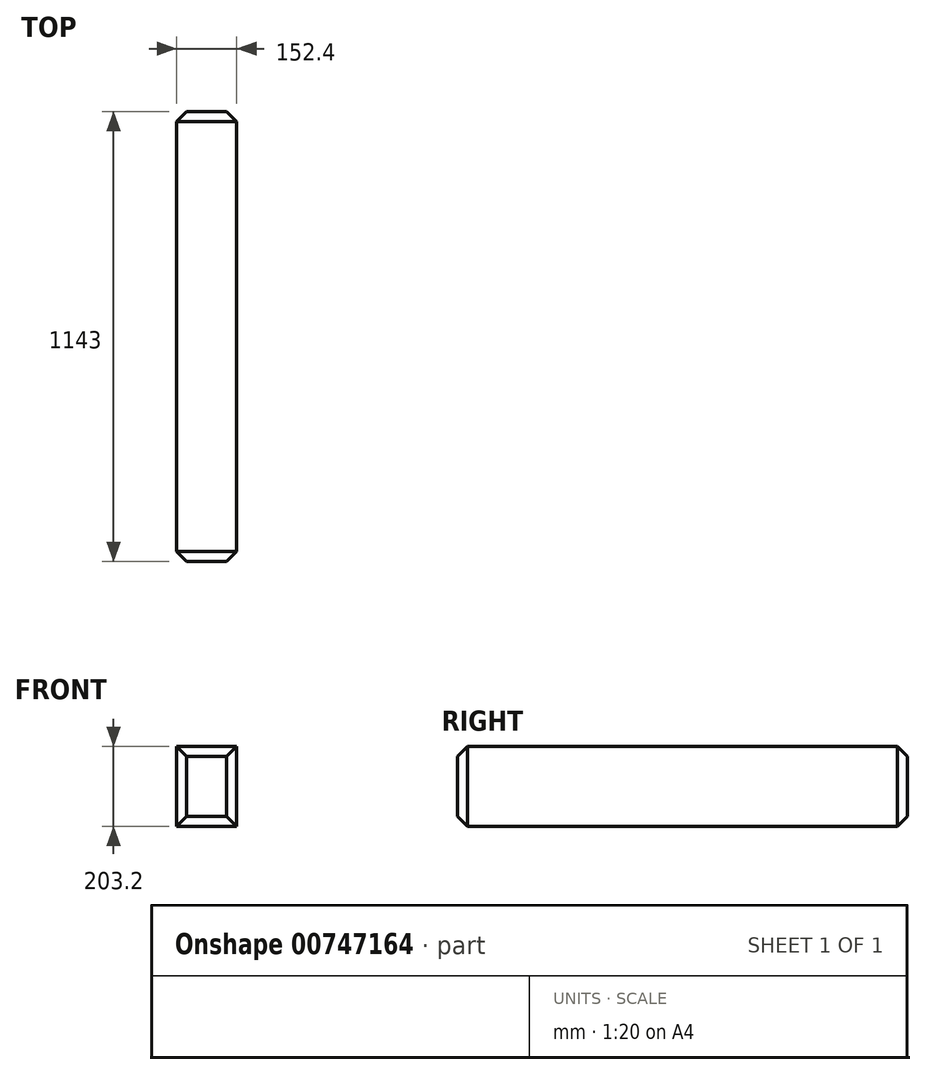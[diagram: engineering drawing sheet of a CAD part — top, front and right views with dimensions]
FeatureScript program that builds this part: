
annotation { "Feature Type Name" : "Feature", "Feature Type Description" : "" }
export const myFeature = defineFeature(function(context is Context, id is Id, definition is map)
    precondition{}
    {
        {
            var Q0;
            Q0=qCreatedBy(makeId("Front.planeOp"),FACE);
            var sketch = newSketch(context, id + "F0", { "sketchPlane" : qUnion([Q0])});
            skLineSegment(sketch, "E0.bottom", {"start": v(-136.78, 154.94) * mm, "end": v(15.62, 154.94) * mm});
            skLineSegment(sketch, "E0.top", {"start": v(-136.78, -48.26) * mm, "end": v(15.62, -48.26) * mm});
            skLineSegment(sketch, "E0.left", {"start": v(-136.78, 154.94) * mm, "end": v(-136.78, -48.26) * mm});
            skLineSegment(sketch, "E0.right", {"start": v(15.62, 154.94) * mm, "end": v(15.62, -48.26) * mm});
            skSolve(sketch);
        }
        {
            var Q0;
            Q0 = qSketchRegion(id + "F0", true);
            extrude(context, id + "F1", {"entities" : qUnion([Q0]), "oppositeDirection" : true, "depth" : 1143 * mm, "offsetDistance" : 25.4 * mm});
        }
        {
            var Q0;
            Q0=makeQuery(id+"F1.opExtrude","CAP_EDGE",EDGE,{"disambiguationData":[OSD([sQuery(id+"F0.wireOp",EDGE,"E0.bottom")])],"isStart":true});
            chamfer(context, id + "F2", {"entities" : qUnion([Q0]), "width" : 25.4 * mm, "tangentPropagation" : true});
        }
        {
            var Q0;
            Q0=makeQuery(id+"F1.opExtrude","CAP_EDGE",EDGE,{"disambiguationData":[OSD([sQuery(id+"F0.wireOp",EDGE,"E0.left")])],"isStart":true});
            var Q1;
            Q1=makeQuery(id+"F1.opExtrude","CAP_EDGE",EDGE,{"disambiguationData":[OSD([sQuery(id+"F0.wireOp",EDGE,"E0.top")])],"isStart":true});
            var Q2;
            Q2=makeQuery(id+"F1.opExtrude","CAP_EDGE",EDGE,{"disambiguationData":[OSD([sQuery(id+"F0.wireOp",EDGE,"E0.right")])],"isStart":true});
            chamfer(context, id + "F3", {"entities" : qUnion([Q0, Q1, Q2]), "width" : 25.4 * mm, "tangentPropagation" : true});
        }
        {
            var Q0;
            Q0=makeQuery(id+"F1.opExtrude","CAP_EDGE",EDGE,{"disambiguationData":[OSD([sQuery(id+"F0.wireOp",EDGE,"E0.bottom")])],"isStart":false});
            var Q1;
            Q1=makeQuery(id+"F1.opExtrude","CAP_EDGE",EDGE,{"disambiguationData":[OSD([sQuery(id+"F0.wireOp",EDGE,"E0.right")])],"isStart":false});
            var Q2;
            Q2=makeQuery(id+"F1.opExtrude","CAP_EDGE",EDGE,{"disambiguationData":[OSD([sQuery(id+"F0.wireOp",EDGE,"E0.top")])],"isStart":false});
            var Q3;
            Q3=makeQuery(id+"F1.opExtrude","CAP_EDGE",EDGE,{"disambiguationData":[OSD([sQuery(id+"F0.wireOp",EDGE,"E0.left")])],"isStart":false});
            chamfer(context, id + "F4", {"entities" : qUnion([Q0, Q1, Q2, Q3]), "width" : 25.4 * mm, "tangentPropagation" : true});
        }
    });
